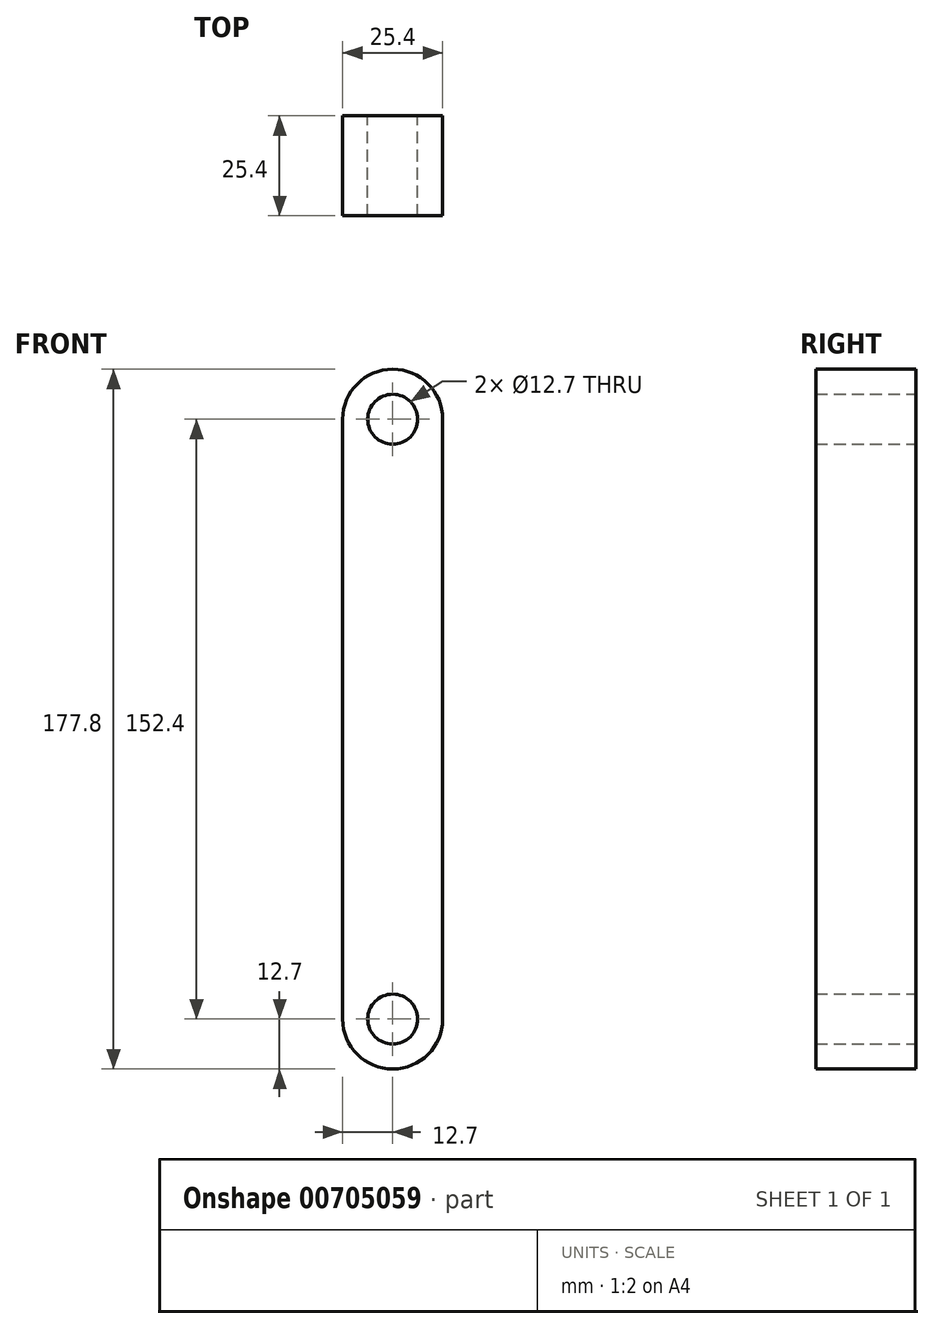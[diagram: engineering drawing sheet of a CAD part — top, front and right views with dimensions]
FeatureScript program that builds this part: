
annotation { "Feature Type Name" : "Feature", "Feature Type Description" : "" }
export const myFeature = defineFeature(function(context is Context, id is Id, definition is map)
    precondition{}
    {
        {
            var Q0;
            Q0=qCreatedBy(makeId("Front.planeOp"),FACE);
            var sketch = newSketch(context, id + "F0", { "sketchPlane" : qUnion([Q0])});
            skLineSegment(sketch, "E0.bottom", {"start": v(0, 0) * mm, "end": v(25.4, 0) * mm});
            skLineSegment(sketch, "E0.top", {"start": v(0, 177.8) * mm, "end": v(25.4, 177.8) * mm});
            skLineSegment(sketch, "E0.left", {"start": v(0, 0) * mm, "end": v(0, 177.8) * mm});
            skLineSegment(sketch, "E0.right", {"start": v(25.4, 0) * mm, "end": v(25.4, 177.8) * mm});
            skPoint(sketch, "E1", {"position": v(12.7, 177.8) * mm});
            skPoint(sketch, "E2", {"position": v(12.7, 165.1) * mm});
            skPoint(sketch, "E3", {"position": v(12.7, 12.7) * mm});
            skCircle(sketch, "E4", {"center": v(12.7, 12.7) * mm, "radius": 6.35 * mm});
            skCircle(sketch, "E5", {"center": v(12.7, 165.1) * mm, "radius": 6.35 * mm});
            skSolve(sketch);
        }
        {
            var Q0;
            Q0 = qSketchRegion(id + "F0", true);
            extrude(context, id + "F1", {"entities" : qUnion([Q0]), "depth" : 25.4 * mm, "offsetDistance" : 25.4 * mm});
        }
        {
            var Q0;
            Q0=makeQuery(id+"F1.opExtrude","SWEPT_EDGE",EDGE,{"disambiguationData":[OSD([sQuery(id+"F0.wireOp",EDGE,"E0.top"),sQuery(id+"F0.wireOp",EDGE,"E0.right")])]});
            var Q1;
            Q1=makeQuery(id+"F1.opExtrude","SWEPT_EDGE",EDGE,{"disambiguationData":[OSD([sQuery(id+"F0.wireOp",EDGE,"E0.top"),sQuery(id+"F0.wireOp",EDGE,"E0.left")])]});
            var Q2;
            Q2=makeQuery(id+"F1.opExtrude","SWEPT_EDGE",EDGE,{"disambiguationData":[OSD([sQuery(id+"F0.wireOp",EDGE,"E0.bottom"),sQuery(id+"F0.wireOp",EDGE,"E0.right")])]});
            var Q3;
            Q3=makeQuery(id+"F1.opExtrude","SWEPT_EDGE",EDGE,{"disambiguationData":[OSD([sQuery(id+"F0.wireOp",EDGE,"E0.bottom"),sQuery(id+"F0.wireOp",EDGE,"E0.left")])]});
            fillet(context, id + "F2", {"entities" : qUnion([Q0, Q1, Q2, Q3]), "radius" : 12.7 * mm, "tangentPropagation" : true, "allowEdgeOverflow" : false});
        }
    });
